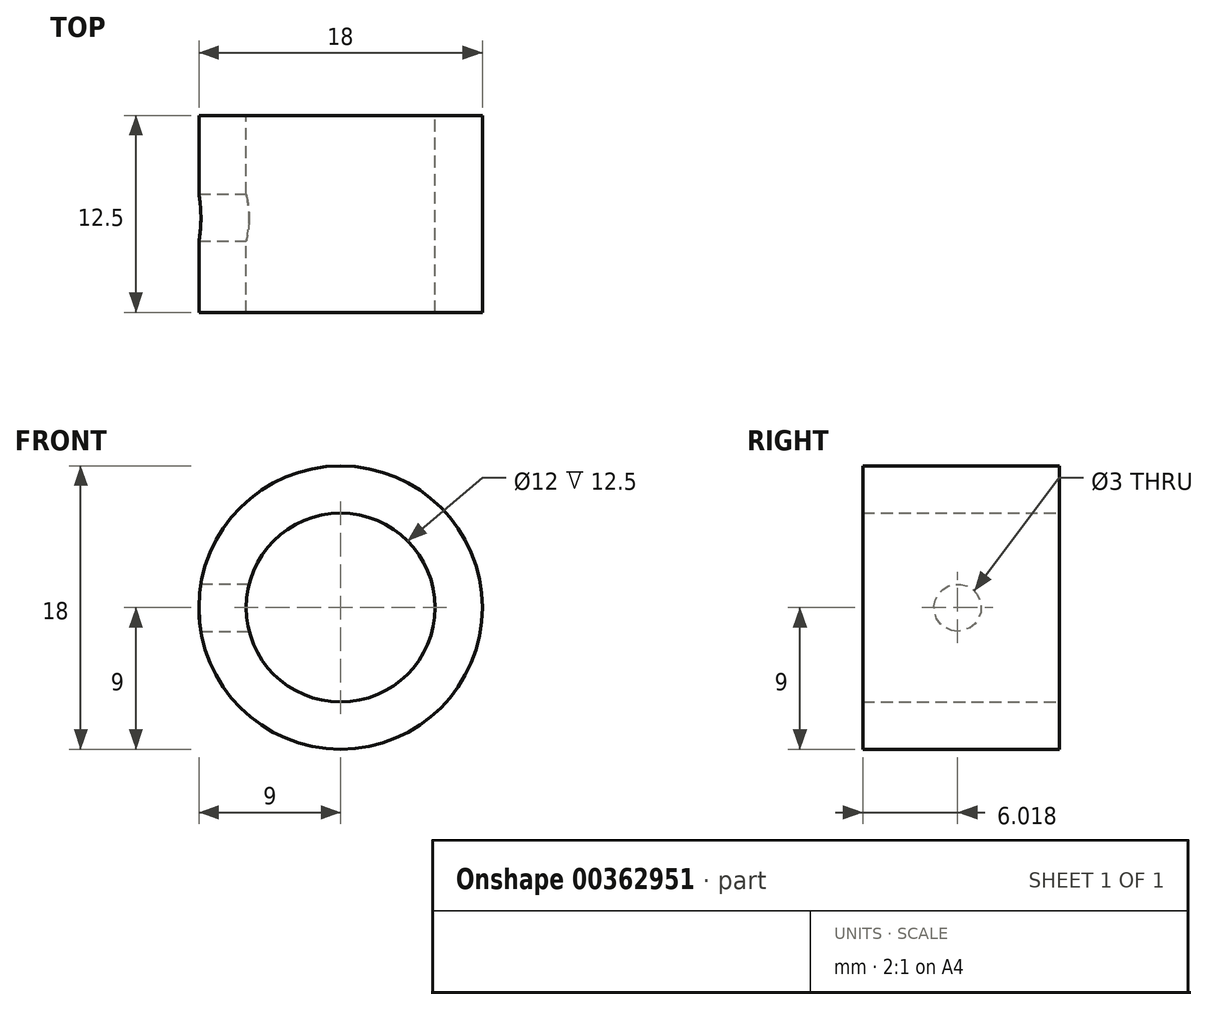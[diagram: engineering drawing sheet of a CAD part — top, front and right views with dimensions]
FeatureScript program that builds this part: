
annotation { "Feature Type Name" : "Feature", "Feature Type Description" : "" }
export const myFeature = defineFeature(function(context is Context, id is Id, definition is map)
    precondition{}
    {
        {
            var Q0;
            Q0=qCreatedBy(makeId("Front.planeOp"),FACE);
            var sketch = newSketch(context, id + "F0", { "sketchPlane" : qUnion([Q0])});
            skCircle(sketch, "E0", {"center": v(0, 0) * mm, "radius": 6 * mm});
            skCircle(sketch, "E1", {"center": v(0, 0) * mm, "radius": 9 * mm});
            skSolve(sketch);
        }
        {
            var Q0;
            Q0=makeQuery(id+"F0.imprint","IMPRINT",FACE,{"disambiguationData":[TD([[makeQuery(id+"F0.imprint","IMPRINT",EDGE,{"derivedFrom":sQuery(id+"F0.wireOp",EDGE,"E0")}),-1.0]])]});
            extrude(context, id + "F1", {"entities" : qUnion([Q0]), "depth" : 12.5 * mm});
        }
        {
            var Q0;
            Q0=qCreatedBy(makeId("Right.planeOp"),FACE);
            var sketch = newSketch(context, id + "F2", { "sketchPlane" : qUnion([Q0])});
            skCircle(sketch, "E2", {"center": v(-6.48, 0) * mm, "radius": 1.77 * mm});
            skSolve(sketch);
        }
        {
            var Q0;
            Q0=sQuery(id+"F2.wireOp",VERTEX,"E2.center");
            var Q1;
            Q1=makeQuery(id+"F1.opExtrude","SWEPT_BODY",BODY,{"disambiguationData":[OSD([sQuery(id+"F0.wireOp",EDGE,"E0"),sQuery(id+"F0.wireOp",EDGE,"E1")])]});
            hole(context, id + "F3", {"style" : HoleStyle.SIMPLE, "endStyle" : HoleEndStyle.BLIND, "holeDiameter" : 3 * mm, "holeDepth" : 12 * mm, "isTappedThrough" : true, "tappedDepth" : 12 * mm, "tapClearance" : 3, "locations" : qUnion([Q0]), "scope" : qUnion([Q1])});
        }
    });
